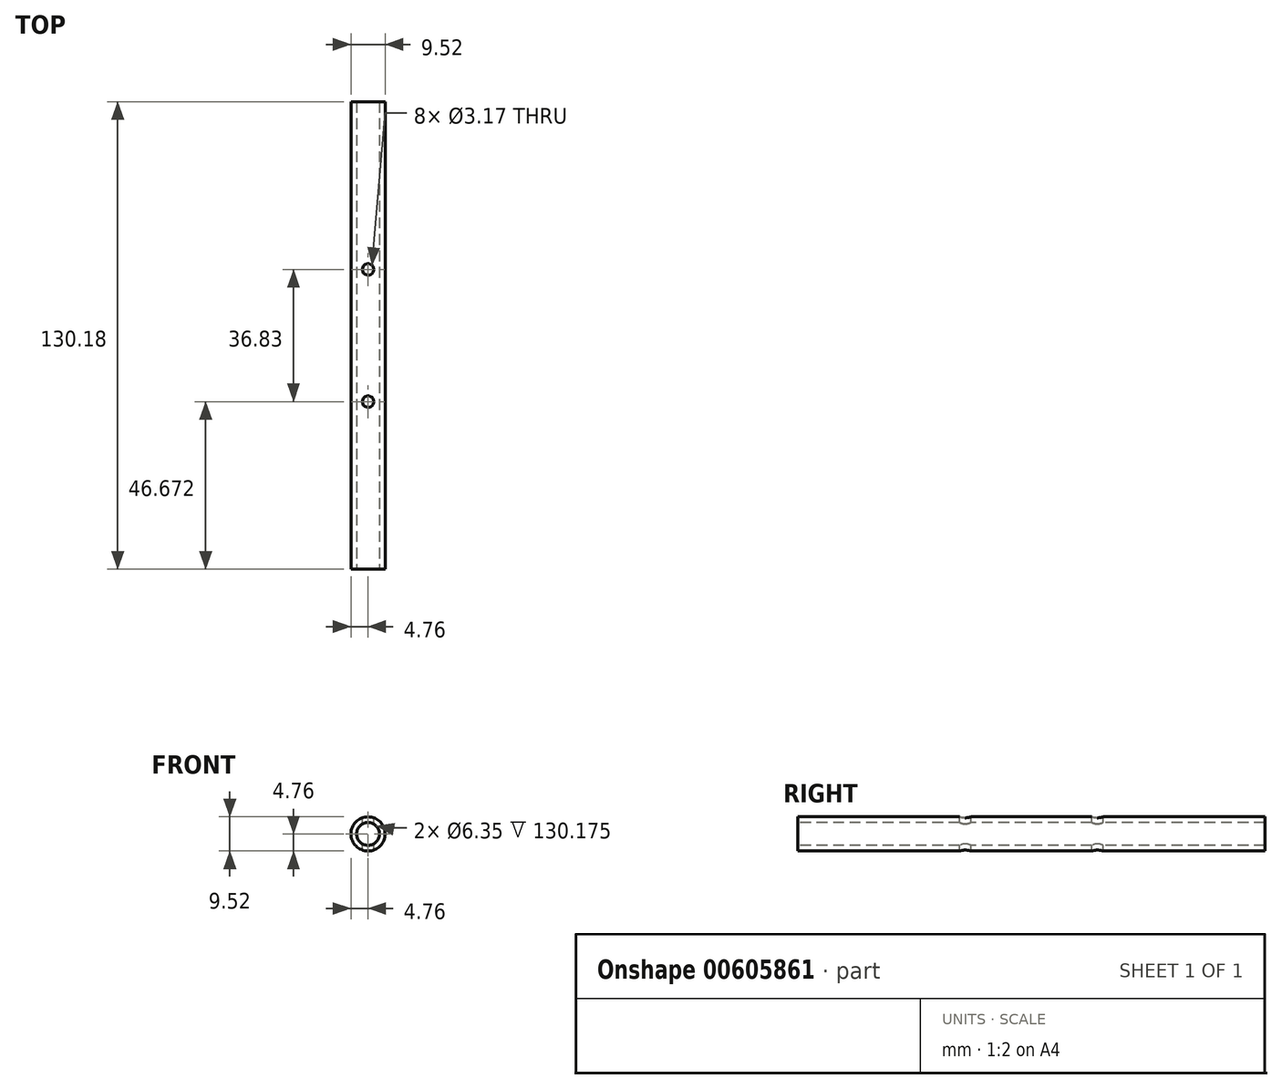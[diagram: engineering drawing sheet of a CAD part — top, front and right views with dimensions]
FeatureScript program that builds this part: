
annotation { "Feature Type Name" : "Feature", "Feature Type Description" : "" }
export const myFeature = defineFeature(function(context is Context, id is Id, definition is map)
    precondition{}
    {
        {
            var Q0;
            Q0=qCreatedBy(makeId("Front.planeOp"),FACE);
            var sketch = newSketch(context, id + "F0", { "sketchPlane" : qUnion([Q0])});
            skCircle(sketch, "E0", {"center": v(0, 0) * mm, "radius": 4.76 * mm});
            skSolve(sketch);
        }
        {
            var Q0;
            Q0=makeQuery(id+"F0.imprint","IMPRINT",FACE,{"disambiguationData":[TD([[makeQuery(id+"F0.imprint","IMPRINT",EDGE,{"derivedFrom":sQuery(id+"F0.wireOp",EDGE,"E0")}),1.0]])]});
            extrude(context, id + "F1", {"entities" : qUnion([Q0]), "oppositeDirection" : true, "depth" : 130.17 * mm, "offsetDistance" : 25.4 * mm});
        }
        {
            var Q0;
            Q0=makeQuery(id+"F1.opExtrude","CAP_FACE",FACE,{"disambiguationData":[OSD([sQuery(id+"F0.wireOp",EDGE,"E0")])],"isStart":true});
            var sketch = newSketch(context, id + "F2", { "sketchPlane" : qUnion([Q0])});
            skPoint(sketch, "E1", {"position": v(0, 0) * mm});
            skSolve(sketch);
        }
        {
            var Q0;
            Q0=sQuery(id+"F2.wireOp",VERTEX,"E1");
            var Q1;
            Q1=makeQuery(id+"F1.opExtrude","SWEPT_BODY",BODY,{"disambiguationData":[OSD([sQuery(id+"F0.wireOp",EDGE,"E0")])]});
            hole(context, id + "F3", {"style" : HoleStyle.SIMPLE, "endStyle" : HoleEndStyle.THROUGH, "holeDiameter" : 6.35 * mm, "majorDiameter" : 6.35 * mm, "isTappedThrough" : true, "tappedDepth" : 12.7 * mm, "tapClearance" : 3, "locations" : qUnion([Q0]), "scope" : qUnion([Q1])});
        }
        {
            var Q0;
            Q0=qCreatedBy(makeId("Front.planeOp"),FACE);
            var sketch = newSketch(context, id + "F4", { "sketchPlane" : qUnion([Q0])});
            skLineSegment(sketch, "E2.bottom", {"start": v(191.66, 0) * mm, "end": v(201.19, 0) * mm});
            skLineSegment(sketch, "E2.top", {"start": v(191.66, 9.53) * mm, "end": v(201.19, 9.53) * mm});
            skLineSegment(sketch, "E2.left", {"start": v(191.66, 0) * mm, "end": v(191.66, 9.53) * mm});
            skLineSegment(sketch, "E2.right", {"start": v(201.19, 0) * mm, "end": v(201.19, 9.53) * mm});
            skSolve(sketch);
        }
        {
            var Q0;
            Q0=makeQuery(id+"F4.imprint","IMPRINT",FACE,{"disambiguationData":[TD([[makeQuery(id+"F4.imprint","IMPRINT",EDGE,{"derivedFrom":sQuery(id+"F4.wireOp",EDGE,"E2.bottom")}),1.0]])]});
            extrude(context, id + "F5", {"entities" : qUnion([Q0]), "oppositeDirection" : true, "depth" : 130.17 * mm, "offsetDistance" : 25.4 * mm});
        }
        {
            var Q0;
            Q0=makeQuery(id+"F5.opExtrude","SWEPT_FACE",FACE,{"disambiguationData":[OSD([sQuery(id+"F4.wireOp",EDGE,"E2.top")])]});
            var sketch = newSketch(context, id + "F6", { "sketchPlane" : qUnion([Q0])});
            skPoint(sketch, "E3", {"position": v(196.42, 83.5) * mm});
            skPoint(sketch, "E4", {"position": v(196.42, 46.67) * mm});
            skSolve(sketch);
        }
        {
            var Q0;
            Q0=sQuery(id+"F6.wireOp",VERTEX,"E3");
            var Q1;
            Q1=sQuery(id+"F6.wireOp",VERTEX,"E4");
            var Q2;
            Q2=makeQuery(id+"F5.opExtrude","SWEPT_BODY",BODY,{"disambiguationData":[OSD([sQuery(id+"F4.wireOp",EDGE,"E2.bottom"),sQuery(id+"F4.wireOp",EDGE,"E2.top"),sQuery(id+"F4.wireOp",EDGE,"E2.left"),sQuery(id+"F4.wireOp",EDGE,"E2.right")])]});
            hole(context, id + "F7", {"style" : HoleStyle.SIMPLE, "endStyle" : HoleEndStyle.THROUGH, "holeDiameter" : 3.17 * mm, "majorDiameter" : 6.35 * mm, "isTappedThrough" : true, "tappedDepth" : 12.7 * mm, "tapClearance" : 3, "locations" : qUnion([Q0, Q1]), "scope" : qUnion([Q2])});
        }
        {
            var Q0;
            Q0=makeQuery(id+"F5.opExtrude","SWEPT_EDGE",EDGE,{"disambiguationData":[OSD([sQuery(id+"F4.wireOp",EDGE,"E2.top"),sQuery(id+"F4.wireOp",EDGE,"E2.right")])]});
            var Q1;
            Q1=makeQuery(id+"F5.opExtrude","SWEPT_EDGE",EDGE,{"disambiguationData":[OSD([sQuery(id+"F4.wireOp",EDGE,"E2.top"),sQuery(id+"F4.wireOp",EDGE,"E2.left")])]});
            var Q2;
            Q2=makeQuery(id+"F5.opExtrude","SWEPT_EDGE",EDGE,{"disambiguationData":[OSD([sQuery(id+"F4.wireOp",EDGE,"E2.bottom"),sQuery(id+"F4.wireOp",EDGE,"E2.right")])]});
            var Q3;
            Q3=makeQuery(id+"F5.opExtrude","SWEPT_EDGE",EDGE,{"disambiguationData":[OSD([sQuery(id+"F4.wireOp",EDGE,"E2.bottom"),sQuery(id+"F4.wireOp",EDGE,"E2.left")])]});
            fillet(context, id + "F8", {"entities" : qUnion([Q0, Q1, Q2, Q3]), "radius" : 5.08 * mm, "tangentPropagation" : true, "allowEdgeOverflow" : false});
        }
        {
            var Q0;
            Q0=qCreatedBy(makeId("Top.planeOp"),FACE);
            cPlane(context, id + "F9", {"entities" : qUnion([Q0]), "cplaneType" : CPlaneType.OFFSET, "offset" : 6.6 * mm, "width" : 152.4 * mm, "height" : 152.4 * mm});
        }
        {
            var Q0;
            Q0=qCreatedBy(id+"F9.planeOp",FACE);
            var sketch = newSketch(context, id + "F10", { "sketchPlane" : qUnion([Q0])});
            skLineSegment(sketch, "E5", {"start": v(0, 140.75) * mm, "end": v(3.97, 140.75) * mm});
            skLineSegment(sketch, "E6", {"start": v(0, 0) * mm, "end": v(-4.76, 0) * mm});
            skLineSegment(sketch, "E7", {"start": v(-4.76, 0) * mm, "end": v(-4.76, 130.18) * mm});
            skLineSegment(sketch, "E8", {"start": v(-4.76, 130.18) * mm, "end": v(0, 130.18) * mm});
            skLineSegment(sketch, "E9", {"start": v(0, 130.18) * mm, "end": v(4.76, 130.18) * mm});
            skLineSegment(sketch, "E10", {"start": v(4.76, 130.18) * mm, "end": v(4.76, 0) * mm});
            skPoint(sketch, "E11", {"position": v(0, 51.96) * mm});
            skLineSegment(sketch, "E12", {"start": v(0, 0) * mm, "end": v(4.76, 0) * mm});
            skLineSegment(sketch, "E13", {"start": v(4.76, 65.09) * mm, "end": v(-4.76, 65.09) * mm});
            skPoint(sketch, "E14.endSnap0", {"position": v(0, 65.09) * mm});
            skPoint(sketch, "E15", {"position": v(0, 83.5) * mm});
            skPoint(sketch, "E16", {"position": v(0, 46.67) * mm});
            skSolve(sketch);
        }
        {
            var Q0;
            Q0=sQuery(id+"F10.wireOp",VERTEX,"E15");
            var Q1;
            Q1=sQuery(id+"F10.wireOp",VERTEX,"E16");
            var Q2;
            Q2=makeQuery(id+"F1.opExtrude","SWEPT_BODY",BODY,{"disambiguationData":[OSD([sQuery(id+"F0.wireOp",EDGE,"E0")])]});
            hole(context, id + "F11", {"style" : HoleStyle.SIMPLE, "endStyle" : HoleEndStyle.THROUGH, "holeDiameter" : 3.17 * mm, "majorDiameter" : 6.35 * mm, "isTappedThrough" : true, "tappedDepth" : 12.7 * mm, "tapClearance" : 3, "locations" : qUnion([Q0, Q1]), "scope" : qUnion([Q2])});
        }
        {
            var Q0;
            Q0=makeQuery(id+"F5.opExtrude","SWEPT_BODY",BODY,{"disambiguationData":[OSD([sQuery(id+"F4.wireOp",EDGE,"E2.bottom"),sQuery(id+"F4.wireOp",EDGE,"E2.top"),sQuery(id+"F4.wireOp",EDGE,"E2.left"),sQuery(id+"F4.wireOp",EDGE,"E2.right")])]});
            deleteBodies(context, id + "F12", {"entities" : qUnion([Q0])});
        }
    });
